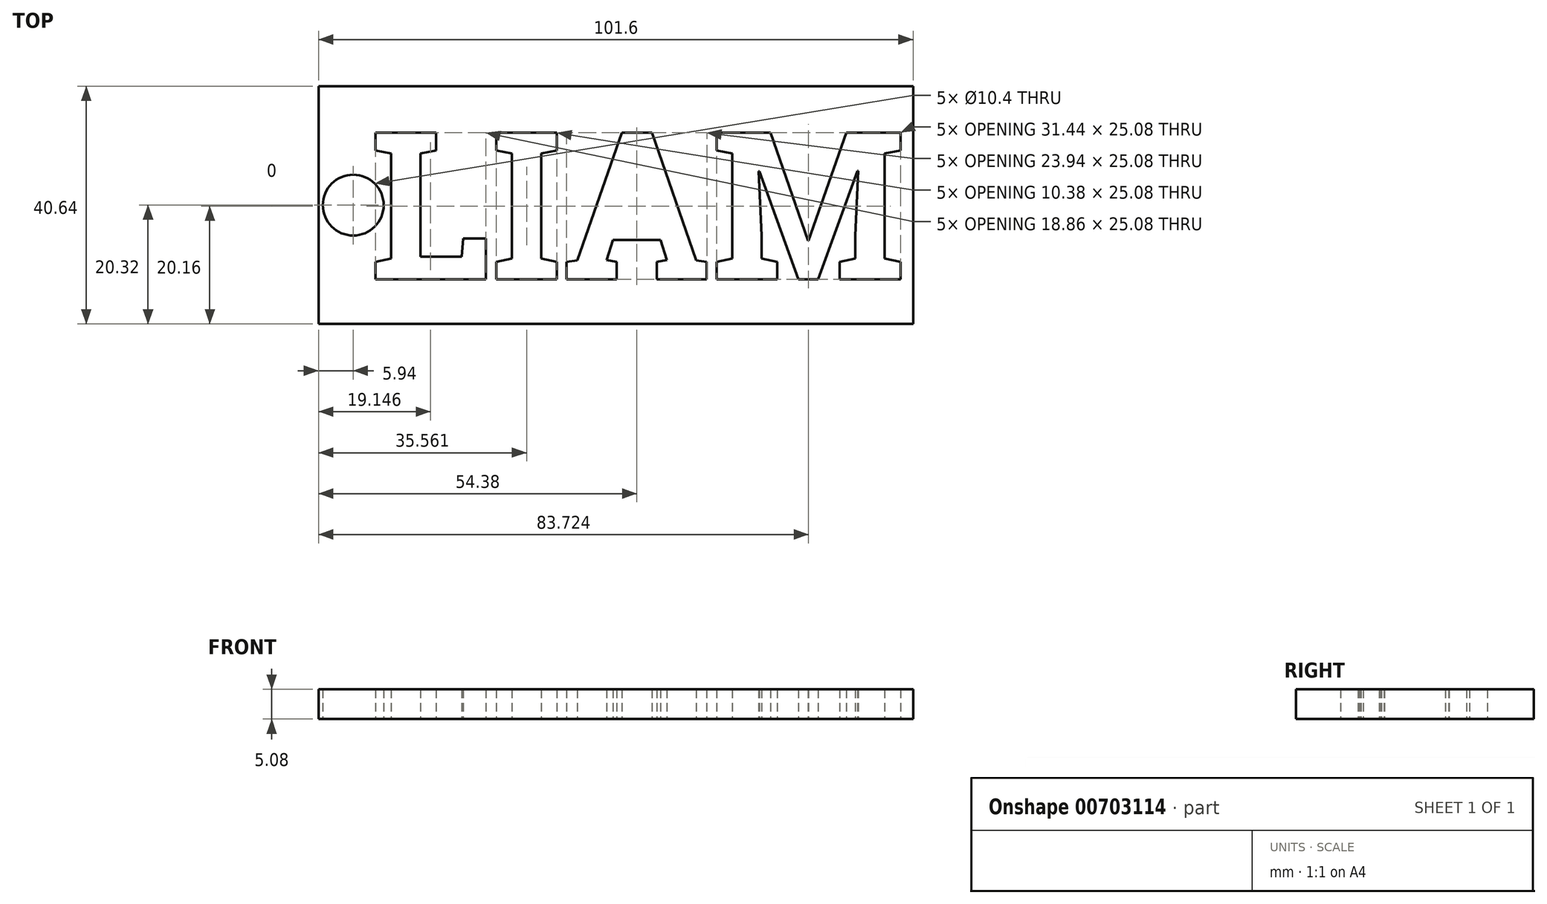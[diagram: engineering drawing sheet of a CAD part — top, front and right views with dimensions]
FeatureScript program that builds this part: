
annotation { "Feature Type Name" : "Feature", "Feature Type Description" : "" }
export const myFeature = defineFeature(function(context is Context, id is Id, definition is map)
    precondition{}
    {
        {
            var Q0;
            Q0=qCreatedBy(makeId("Top.planeOp"),FACE);
            var sketch = newSketch(context, id + "F0", { "sketchPlane" : qUnion([Q0])});
            skLineSegment(sketch, "E0.bottom", {"start": v(50.8, 20.32) * mm, "end": v(-50.8, 20.32) * mm});
            skLineSegment(sketch, "E0.top", {"start": v(50.8, -20.32) * mm, "end": v(-50.8, -20.32) * mm});
            skLineSegment(sketch, "E0.left", {"start": v(50.8, 20.32) * mm, "end": v(50.8, -20.32) * mm});
            skLineSegment(sketch, "E0.right", {"start": v(-50.8, 20.32) * mm, "end": v(-50.8, -20.32) * mm});
            skPoint(sketch, "E0.middle", {"position": v(0, 0) * mm});
            skText(sketch, "E1", { "text": "LIAM", "fontName": "RobotoSlab-Bold.ttf"});
            skCircle(sketch, "E2", {"center": v(-44.86, 0) * mm, "radius": 5.2 * mm});
            const initialGuessF0  = {"E1": [-0.04205, -0.0127, 1, 0, 0.0254]};
            skSetInitialGuess(sketch, initialGuessF0);
            skSolve(sketch);
        }
        {
            var Q0;
            Q0 = qSketchRegion(id + "F0", true);
            extrude(context, id + "F1", {"entities" : qUnion([Q0]), "depth" : 5.08 * mm, "offsetDistance" : 25.4 * mm});
        }
    });
